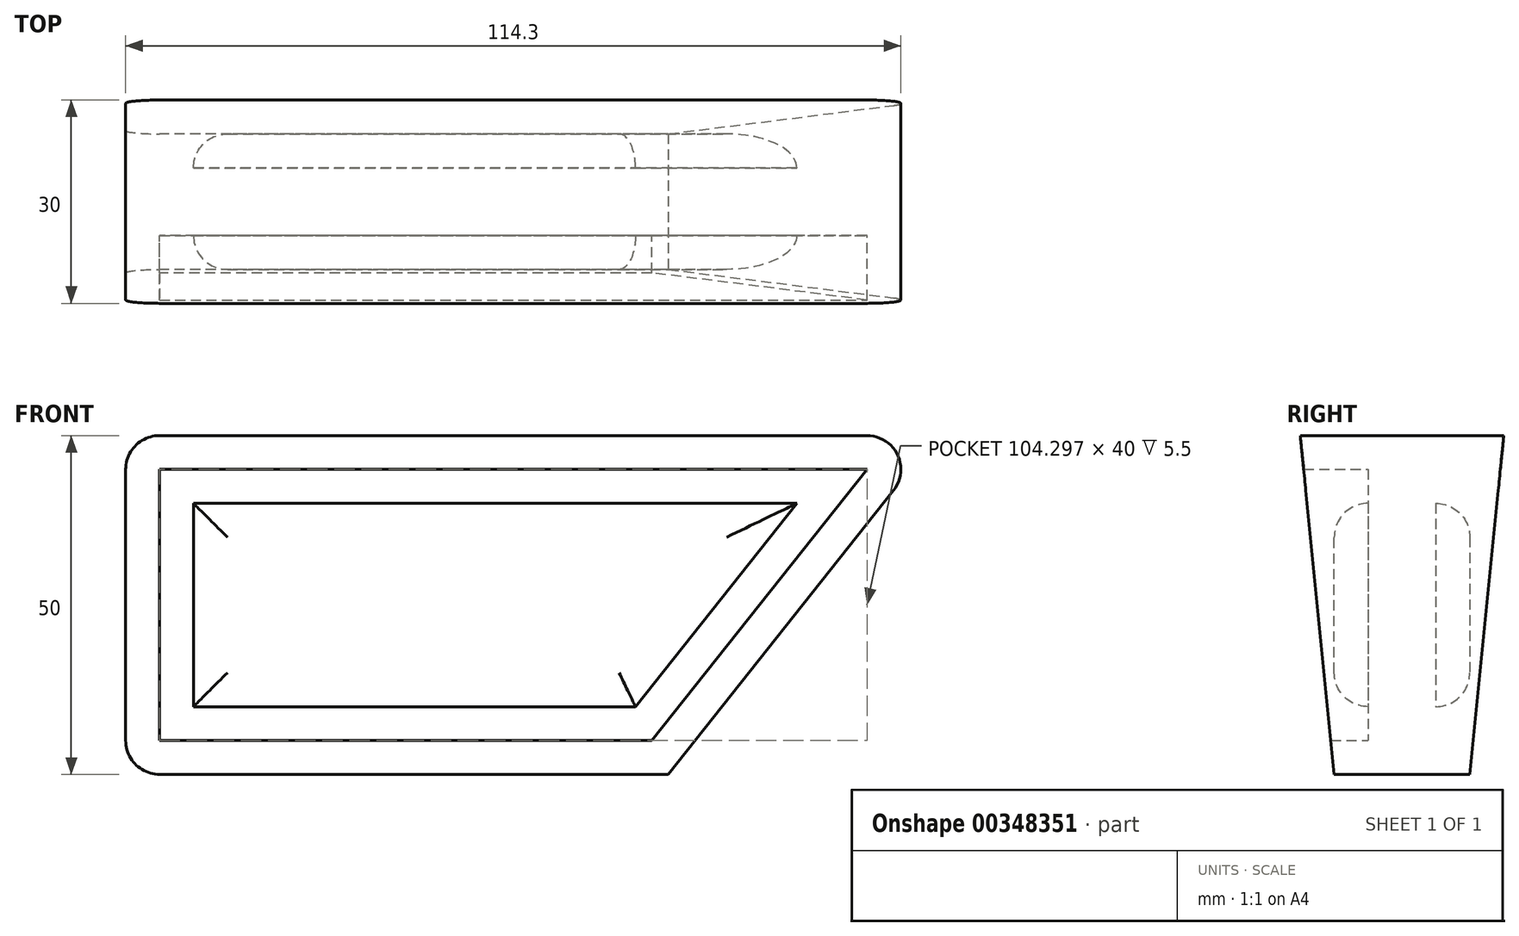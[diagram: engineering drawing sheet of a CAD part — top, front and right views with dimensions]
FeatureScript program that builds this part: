
annotation { "Feature Type Name" : "Feature", "Feature Type Description" : "" }
export const myFeature = defineFeature(function(context is Context, id is Id, definition is map)
    precondition{}
    {
        {
            var Q0;
            Q0=qCreatedBy(makeId("Front.planeOp"),FACE);
            cPlane(context, id + "F0", {"entities" : qUnion([Q0]), "cplaneType" : CPlaneType.OFFSET, "offset" : 5 * mm, "width" : 150 * mm, "height" : 150 * mm});
        }
        {
            var Q0;
            Q0=qCreatedBy(makeId("Right.planeOp"),FACE);
            var sketch = newSketch(context, id + "F1", { "sketchPlane" : qUnion([Q0])});
            skLineSegment(sketch, "E0", {"start": v(0, 0) * mm, "end": v(0, 57.54) * mm, "construction": true});
            skLineSegment(sketch, "E1", {"start": v(0, 0) * mm, "end": v(10, 0) * mm});
            skLineSegment(sketch, "E2", {"start": v(10, 0) * mm, "end": v(15, 50) * mm});
            skLineSegment(sketch, "E3", {"start": v(15, 50) * mm, "end": v(0, 50) * mm});
            skLineSegment(sketch, "E4.MirrorCS", {"start": v(-15, 50) * mm, "end": v(0, 50) * mm});
            skLineSegment(sketch, "E5.MirrorCS", {"start": v(-10, 0) * mm, "end": v(-15, 50) * mm});
            skLineSegment(sketch, "E6.MirrorCS", {"start": v(0, 0) * mm, "end": v(-10, 0) * mm});
            skSolve(sketch);
        }
        {
            var Q0;
            Q0 = qSketchRegion(id + "F1", true);
            extrude(context, id + "F2", {"entities" : qUnion([Q0]), "depth" : 120 * mm});
        }
        {
            var Q0;
            Q0=qCreatedBy(makeId("Front.planeOp"),FACE);
            var sketch = newSketch(context, id + "F3", { "sketchPlane" : qUnion([Q0])});
            skLineSegment(sketch, "E7", {"start": v(80, 0) * mm, "end": v(120, 50.45) * mm});
            skLineSegment(sketch, "E8", {"start": v(80, 0) * mm, "end": v(120, 0) * mm});
            skLineSegment(sketch, "E9", {"start": v(120, 0) * mm, "end": v(120, 50.45) * mm});
            skSolve(sketch);
        }
        {
            var Q0;
            Q0 = qSketchRegion(id + "F3", true);
            extrude(context, id + "F4", {"entities" : qUnion([Q0]), "operationType" : NewBodyOperationType.REMOVE, "endBound" : BoundingType.THROUGH_ALL, "oppositeDirection" : true, "depth" : 25 * mm, "hasSecondDirection" : true, "secondDirectionBound" : SecondDirectionBoundingType.THROUGH_ALL, "secondDirectionOppositeDirection" : false, "secondDirectionDepth" : 25 * mm});
        }
        {
            var Q0;
            Q0=qCreatedBy(id+"F0.planeOp",FACE);
            var sketch = newSketch(context, id + "F5", { "sketchPlane" : qUnion([Q0])});
            skLineSegment(sketch, "E10.0", {"start": v(5, 5) * mm, "end": v(77.58, 5) * mm});
            skLineSegment(sketch, "E10.1", {"start": v(5, 45) * mm, "end": v(5, 5) * mm});
            skLineSegment(sketch, "E10.2", {"start": v(109.3, 45) * mm, "end": v(5, 45) * mm});
            skLineSegment(sketch, "E10.3", {"start": v(77.58, 5) * mm, "end": v(109.3, 45) * mm});
            skSolve(sketch);
        }
        {
            var Q0;
            Q0 = qSketchRegion(id + "F5", true);
            extrude(context, id + "F6", {"entities" : qUnion([Q0]), "operationType" : NewBodyOperationType.REMOVE, "depth" : 25 * mm});
        }
        {
            var Q0;
            Q0=makeQuery(id+"F6.boolean.opBoolean","COPY",FACE,{"derivedFrom":makeQuery(id+"F6.opExtrude","CAP_FACE",FACE,{"disambiguationData":[OSD([sQuery(id+"F5.wireOp",EDGE,"E10.0"),sQuery(id+"F5.wireOp",EDGE,"E10.1"),sQuery(id+"F5.wireOp",EDGE,"E10.2"),sQuery(id+"F5.wireOp",EDGE,"E10.3")])],"isStart":true})});
            var sketch = newSketch(context, id + "F7", { "sketchPlane" : qUnion([Q0])});
            skLineSegment(sketch, "E11.0", {"start": v(10, 10) * mm, "end": v(75.17, 10) * mm});
            skLineSegment(sketch, "E11.1", {"start": v(10, 40) * mm, "end": v(10, 10) * mm});
            skLineSegment(sketch, "E11.2", {"start": v(98.95, 40) * mm, "end": v(10, 40) * mm});
            skLineSegment(sketch, "E11.3", {"start": v(75.17, 10) * mm, "end": v(98.95, 40) * mm});
            skSolve(sketch);
        }
        {
            var Q0;
            Q0 = qSketchRegion(id + "F7", true);
            extrude(context, id + "F8", {"entities" : qUnion([Q0]), "depth" : 5 * mm});
        }
        {
            var Q0;
            Q0=makeQuery(id+"F8.opExtrude","CAP_FACE",FACE,{"disambiguationData":[OSD([sQuery(id+"F7.wireOp",EDGE,"E11.0"),sQuery(id+"F7.wireOp",EDGE,"E11.1"),sQuery(id+"F7.wireOp",EDGE,"E11.2"),sQuery(id+"F7.wireOp",EDGE,"E11.3")])],"isStart":false});
            fillet(context, id + "F9", {"entities" : qUnion([Q0]), "radius" : 5 * mm, "tangentPropagation" : true, "allowEdgeOverflow" : false});
        }
        {
            var Q0;
            Q0=makeQuery(id+"F8.opExtrude","SWEPT_BODY",BODY,{"disambiguationData":[OSD([sQuery(id+"F7.wireOp",EDGE,"E11.0"),sQuery(id+"F7.wireOp",EDGE,"E11.1"),sQuery(id+"F7.wireOp",EDGE,"E11.2"),sQuery(id+"F7.wireOp",EDGE,"E11.3")])]});
            var Q1;
            Q1=qCreatedBy(makeId("Front.planeOp"),FACE);
            mirror(context, id + "F10", {"entities" : qUnion([Q0]), "mirrorPlane" : qUnion([Q1])});
        }
        {
            var Q0;
            Q0=makeQuery(id+"F4.boolean.opBoolean","INTERSECT",EDGE,{"derivedFrom":[makeQuery(id+"F2.opExtrude","SWEPT_FACE",FACE,{"disambiguationData":[OSD([sQuery(id+"F1.wireOp",EDGE,"E3"),sQuery(id+"F1.wireOp",EDGE,"E4.MirrorCS")])]}),makeQuery(id+"F4.opExtrude","SWEPT_FACE",FACE,{"disambiguationData":[OSD([sQuery(id+"F3.wireOp",EDGE,"E7")])]})]});
            var Q1;
            Q1=makeQuery(id+"F4.boolean.opBoolean","COPY",EDGE,{"derivedFrom":makeQuery(id+"F4.opExtrude","SWEPT_EDGE",EDGE,{"disambiguationData":[OSD([sQuery(id+"F3.wireOp",EDGE,"E7"),sQuery(id+"F3.wireOp",EDGE,"E8")])]})});
            var Q2;
            Q2=makeQuery(id+"F2.opExtrude","CAP_EDGE",EDGE,{"disambiguationData":[OSD([sQuery(id+"F1.wireOp",EDGE,"E1"),sQuery(id+"F1.wireOp",EDGE,"E6.MirrorCS")])],"isStart":true});
            var Q3;
            Q3=makeQuery(id+"F2.opExtrude","CAP_EDGE",EDGE,{"disambiguationData":[OSD([sQuery(id+"F1.wireOp",EDGE,"E3"),sQuery(id+"F1.wireOp",EDGE,"E4.MirrorCS")])],"isStart":true});
            fillet(context, id + "F11", {"entities" : qUnion([Q0, Q1, Q2, Q3]), "radius" : 5 * mm, "tangentPropagation" : true, "allowEdgeOverflow" : false});
        }
    });
